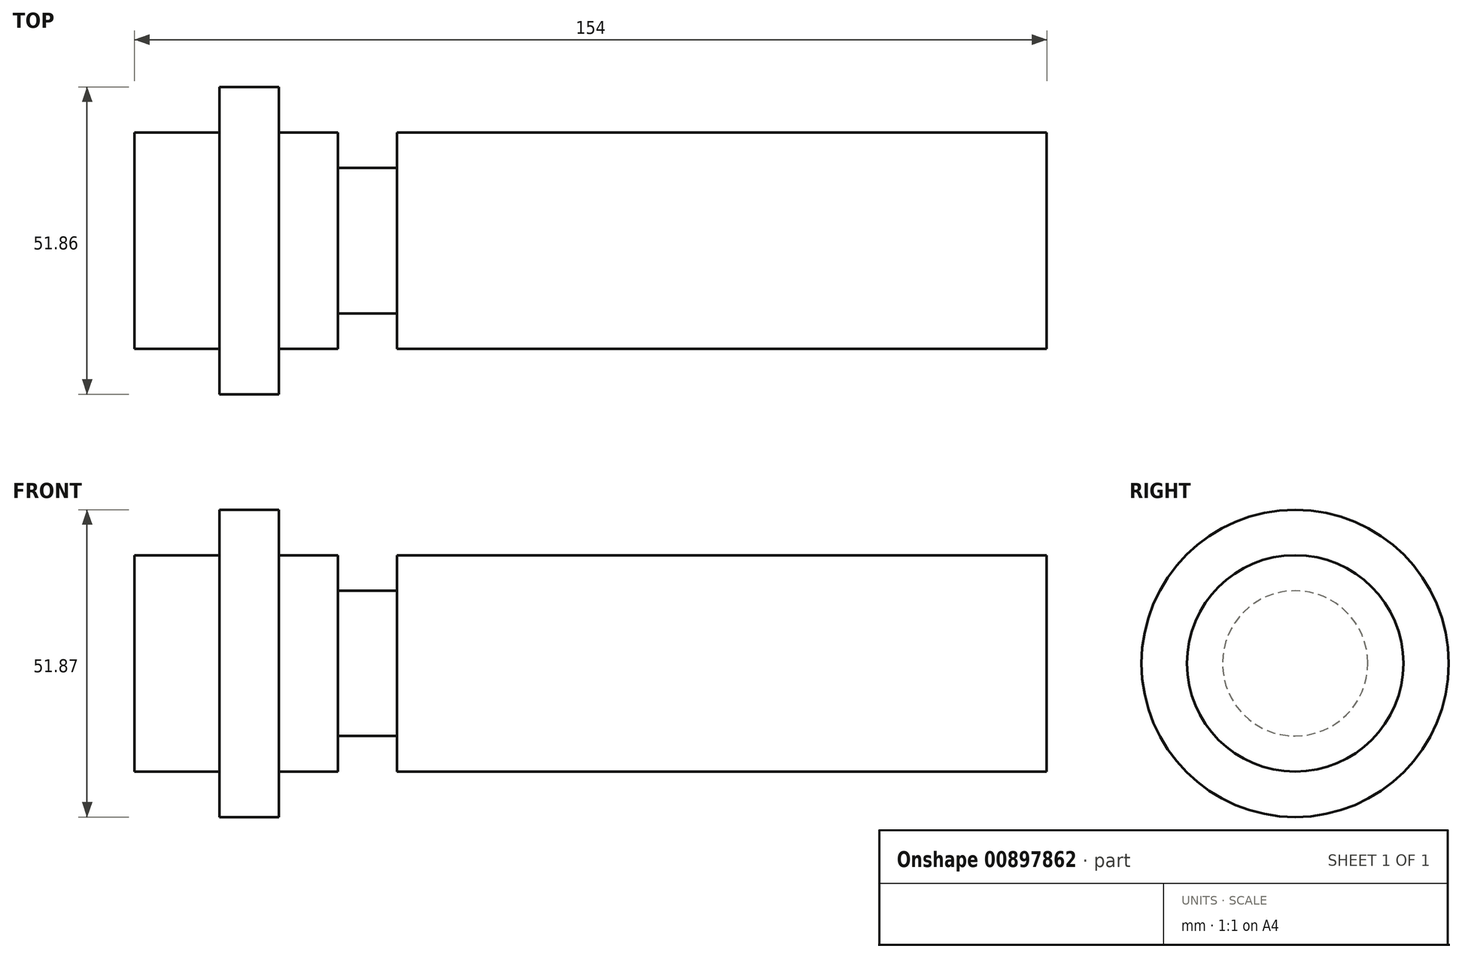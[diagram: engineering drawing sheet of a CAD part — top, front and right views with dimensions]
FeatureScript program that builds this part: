
annotation { "Feature Type Name" : "Feature", "Feature Type Description" : "" }
export const myFeature = defineFeature(function(context is Context, id is Id, definition is map)
    precondition{}
    {
        {
            var Q0;
            Q0=qCreatedBy(makeId("Front.planeOp"),FACE);
            var sketch = newSketch(context, id + "F0", { "sketchPlane" : qUnion([Q0])});
            skLineSegment(sketch, "E0", {"start": v(-103.3, 5.54) * mm, "end": v(134.34, 5.54) * mm, "construction": true});
            skLineSegment(sketch, "E1.bottom", {"start": v(-80.11, 23.81) * mm, "end": v(-45.78, 23.81) * mm});
            skLineSegment(sketch, "E1.top", {"start": v(-80.11, 5.54) * mm, "end": v(73.89, 5.54) * mm});
            skLineSegment(sketch, "E1.left", {"start": v(-80.11, 23.81) * mm, "end": v(-80.11, 5.54) * mm});
            skLineSegment(sketch, "E1.right", {"start": v(73.89, 23.81) * mm, "end": v(73.89, 5.54) * mm});
            skLineSegment(sketch, "E2.bottom", {"start": v(-65.78, 23.81) * mm, "end": v(-55.78, 23.81) * mm});
            skLineSegment(sketch, "E2.top", {"start": v(-65.78, 31.48) * mm, "end": v(-55.78, 31.48) * mm});
            skLineSegment(sketch, "E2.left", {"start": v(-65.78, 23.81) * mm, "end": v(-65.78, 31.48) * mm});
            skLineSegment(sketch, "E2.right", {"start": v(-55.78, 23.81) * mm, "end": v(-55.78, 31.48) * mm});
            skLineSegment(sketch, "E3.top", {"start": v(-45.78, 17.81) * mm, "end": v(-35.78, 17.81) * mm});
            skLineSegment(sketch, "E3.left", {"start": v(-45.78, 23.81) * mm, "end": v(-45.78, 17.81) * mm});
            skLineSegment(sketch, "E3.right", {"start": v(-35.78, 23.81) * mm, "end": v(-35.78, 17.81) * mm});
            skLineSegment(sketch, "E4.trimOffspring", {"start": v(-35.78, 23.81) * mm, "end": v(73.89, 23.81) * mm});
            skSolve(sketch);
        }
        {
            var Q0;
            Q0 = qSketchRegion(id + "F0", true);
            var Q1;
            Q1=sQuery(id+"F0.wireOp",EDGE,"E0");
            revolve(context, id + "F1", {"surfaceOperationType" : NewSurfaceOperationType.NEW, "entities" : qUnion([Q0]), "axis" : qUnion([Q1]), "revolveType" : RevolveType.FULL});
        }
    });
